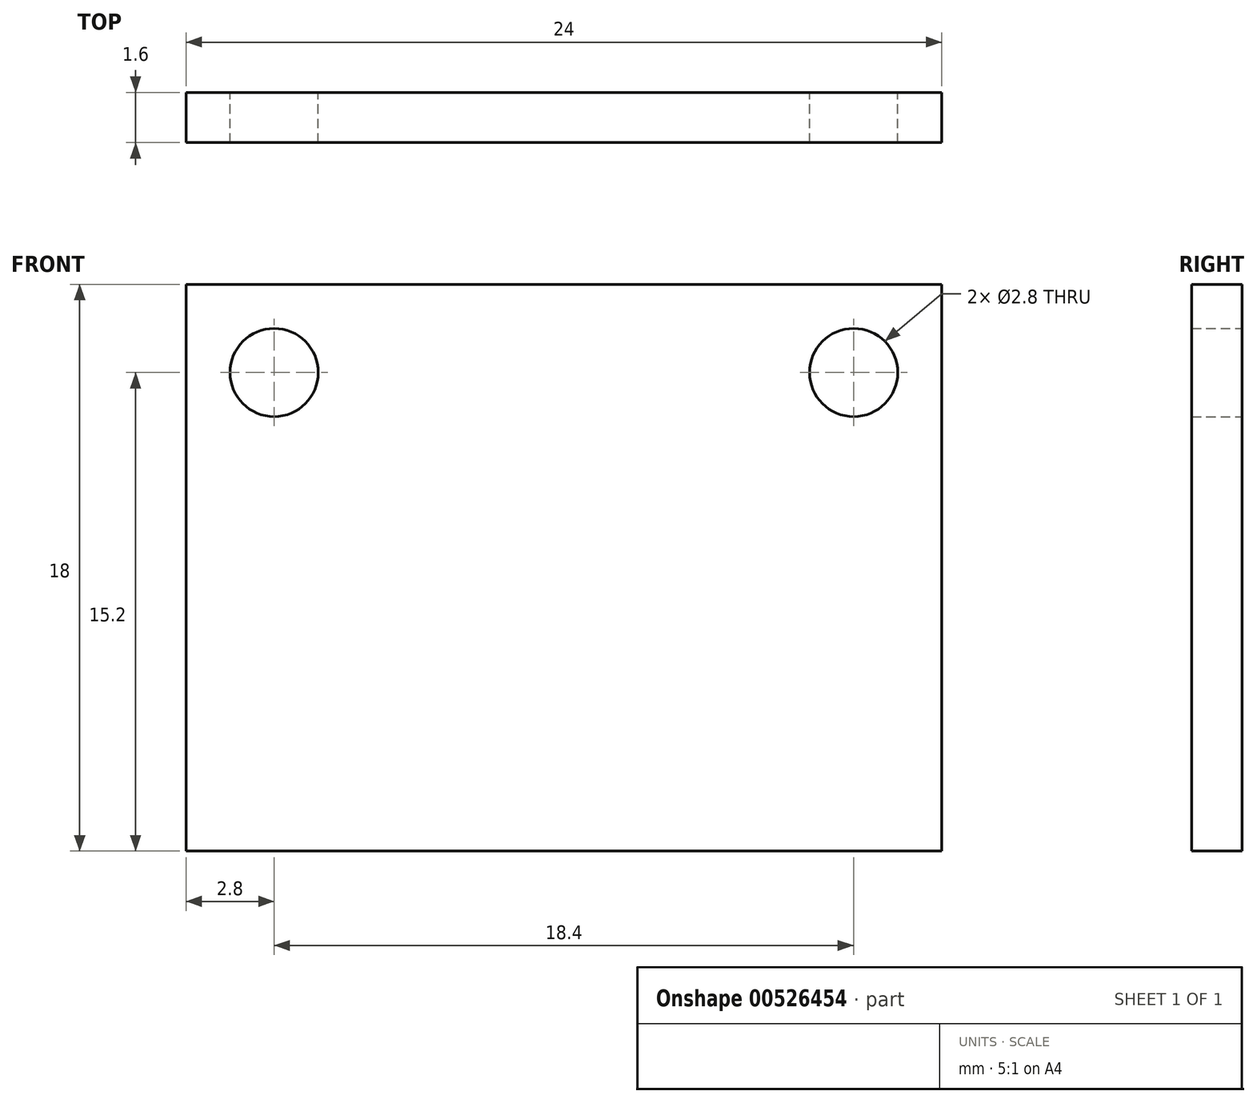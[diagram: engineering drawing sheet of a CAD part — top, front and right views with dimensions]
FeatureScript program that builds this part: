
annotation { "Feature Type Name" : "Feature", "Feature Type Description" : "" }
export const myFeature = defineFeature(function(context is Context, id is Id, definition is map)
    precondition{}
    {
        {
            var Q0;
            Q0=qCreatedBy(makeId("Front.planeOp"),FACE);
            var sketch = newSketch(context, id + "F0", { "sketchPlane" : qUnion([Q0])});
            skLineSegment(sketch, "E0.bottom", {"start": v(-12, 9) * mm, "end": v(12, 9) * mm});
            skLineSegment(sketch, "E0.top", {"start": v(-12, -9) * mm, "end": v(12, -9) * mm});
            skLineSegment(sketch, "E0.left", {"start": v(-12, 9) * mm, "end": v(-12, -9) * mm});
            skLineSegment(sketch, "E0.right", {"start": v(12, 9) * mm, "end": v(12, -9) * mm});
            skPoint(sketch, "E0.middle", {"position": v(0, 0) * mm});
            skCircle(sketch, "E1", {"center": v(-9.2, 6.2) * mm, "radius": 1.4 * mm});
            skCircle(sketch, "E2", {"center": v(9.2, 6.2) * mm, "radius": 1.4 * mm});
            skLineSegment(sketch, "E3", {"start": v(-9.2, 6.2) * mm, "end": v(9.2, 6.2) * mm, "construction": true});
            skLineSegment(sketch, "E4", {"start": v(0, 0) * mm, "end": v(0, 6.2) * mm, "construction": true});
            skSolve(sketch);
        }
        {
            var Q0;
            Q0 = qSketchRegion(id + "F0", true);
            extrude(context, id + "F1", {"entities" : qUnion([Q0]), "depth" : 1.6 * mm, "offsetDistance" : 25 * mm});
        }
    });
